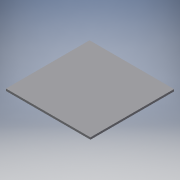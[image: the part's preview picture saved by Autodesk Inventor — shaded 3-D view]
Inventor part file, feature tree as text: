
AUTODESK INVENTOR PART (.ipt)
format: ipt  version: 2018.2 (Build 222227000, 227)  size: 89,600 bytes
history: native  units: in
note: dims shown in document units (in); Inventor stores cm internally (conversion verified against a paired STEP export)
features: extrude x1, sketch x1
ambient origin geometry x8: Origin, YZ Plane, XZ Plane, XY Plane, X Axis, Y Axis, Z Axis, Center Point
bodies: Solid1 (feature_tree)
feature tree (2):
  extrude  "Extrusion1"  Depth=30.898in
  sketch  "Sketch1"  dims[d0=31.225in d1=30.898in d2=0.75in d3=0.0in]
